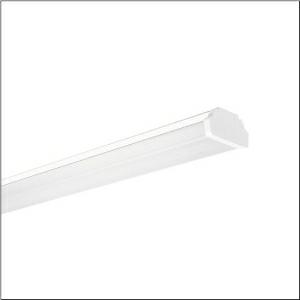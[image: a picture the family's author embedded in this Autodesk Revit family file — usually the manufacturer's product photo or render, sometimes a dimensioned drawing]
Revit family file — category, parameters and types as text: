
# Revit family: dus_31_gen_2_53bd812cv6a5d2_532a
name_source: partatom
category: Lighting Fixtures
units: mm (PartAtom-declared; Revit-internal decimal feet)

## family parameters
Cut with Voids When Loaded = No
Host = Face
Light Source = No
Part Type = Normal
Room Calculation Point = No
Round Connector Dimension = Use Diameter
Shared = No

## types (1)
- --- (1 x LED, 10550 lm, 56.5 W, 6500K)
    Apparent Load = 57 VA
    CIE Flux Codes = 47 80 95 93 100
    Color Rendering = 80
    Color Temperature = 6500K
    Default Elevation = 1800 mm
    Description = DUS 31 Gen.2, luminaire insert, of sheet steel, coil coated, white, length: 1.535mm, width: 81mm, height: 90mm, 5x system unit, system units: 307mm, LED rated luminous flux: 10.550lm, light colour: 865, SDCM (Standard Deviation of Colour Matching)MacAdam ≤ 3 SDCM (initial), control gear: ON/OFF Multilumen, CLOi, with plug, 3-pole, with phase selection, mains connection: 220..240V, AC, 50/60Hz, start of lifetime: 57W, end of service life: 68W, through-wiring accessed according to module size, primary optical cover: cover, of PMMA, light emission: direct distribution, primary light characteristic: symmetric, protection rating (complete): IP20, protection rating (LED compartment): IP50, insulation class (complete): insulation class I (protective earthing), certification: CE, ENEC, VDE, UKCA, impact resistance: IK03, permissible ambient temperature for indoor applications: -35..+40°C, corresponds to IFS (International Featured Standards) requirements for safety and quality in the food industry, reducing of maximum allowable ambient temperature of 5°C with ceiling mounting, packaging unit: 1 piece
    Height = 95 mm
    Lamp = 1 x LED
    Lamp Light Flux = 10550 lm
    Lamp Power = 56.5 W
    Lamp count = 1
    Length = 1535 mm
    Luminous efficacy = 187 lm/W
    Manufacturer = Siteco
    ModVariant = No
    Model = 53BD812CV6A5D2
    Mounting Place = Ceiling
    Mounting Type = Pendant
    Number of Poles = 1
    OnlyDefault = Yes
    Power Factor = 1
    Product Name = DUS 31 Gen.2
    Product group = luminaire insert | ceiling pendant
    ProductGroupID = 901
    Protection Class = Protection class I
    Protection Degree = IP 20
    RLX_Detail_Level = 1
    RLX_Emergency_Light_Flux = 0 lm
    RLX_Emergency_Type = 0
    RLX_Emergency_Type_DB = No
    RlxData = <blob elided: 29817 chars, md5=413bd370>
    Socket = socket
    Standby Power = 0 W
    System Light Flux = 10550 lm
    System Power = 57 W
    Type Comments = factory setting: luminous flux: 100 % | (A | C | E) | 133 mA
    Type Image = l_1319596.jpg
    URL = http://relux.com
    VarID = @adj_040771
    Voltage = 0 V
    Weight = 0.00 kg
    Width = 81 mm

## geometry (parser evidence)
native form markers: Blend x4, Sweep x14
no freeform markers — native parametric forms only
